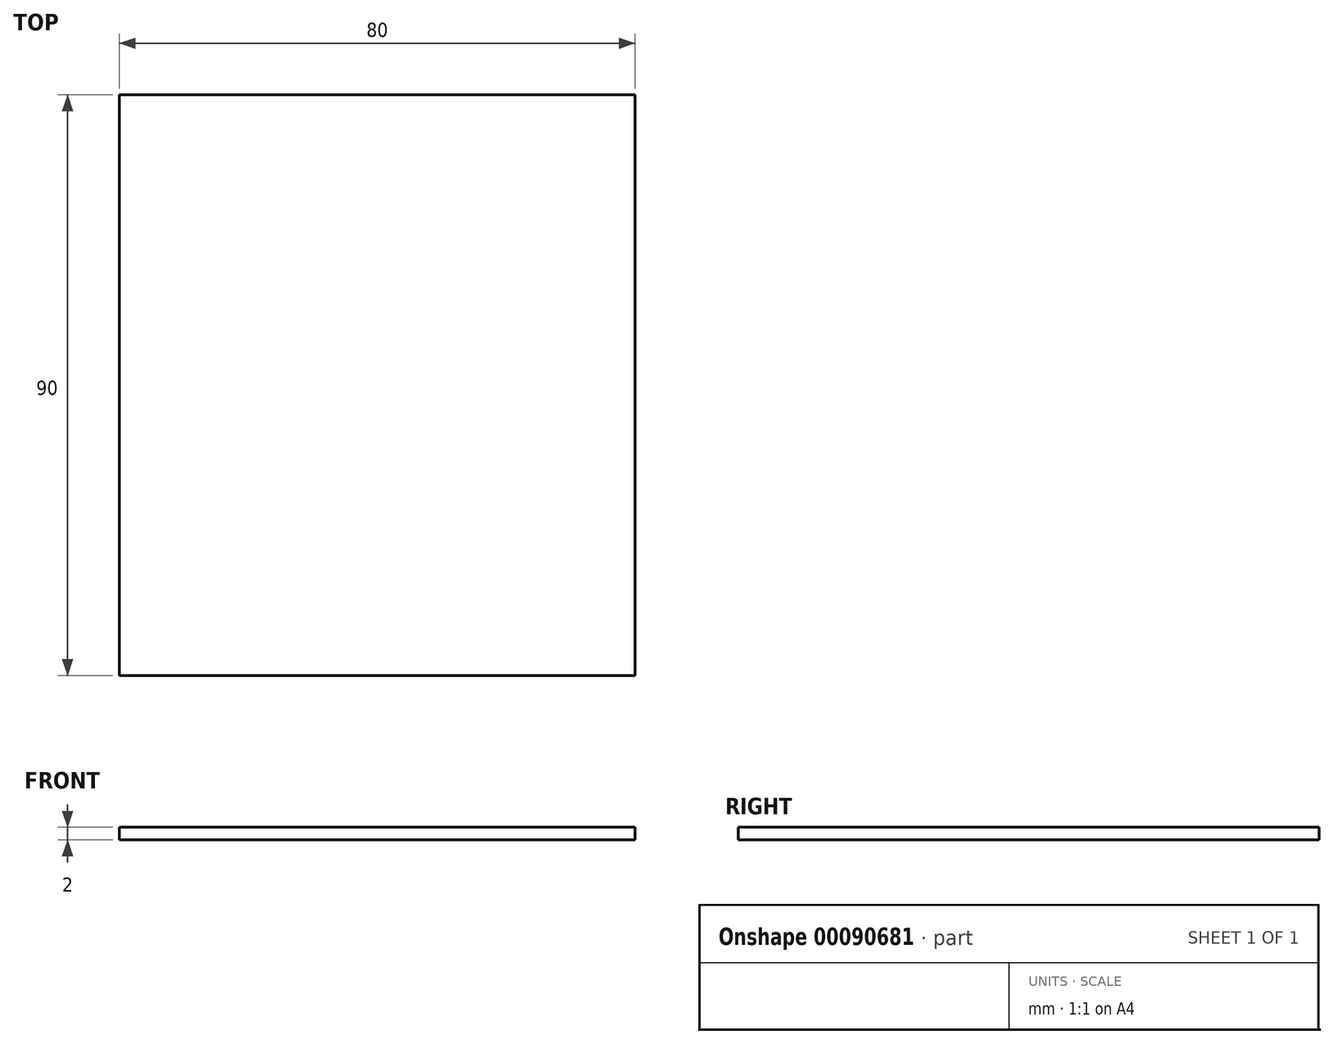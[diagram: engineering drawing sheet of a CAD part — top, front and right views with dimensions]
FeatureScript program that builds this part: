
annotation { "Feature Type Name" : "Feature", "Feature Type Description" : "" }
export const myFeature = defineFeature(function(context is Context, id is Id, definition is map)
    precondition{}
    {
        {
            var Q0;
            Q0=qCreatedBy(makeId("Top.planeOp"),FACE);
            var sketch = newSketch(context, id + "F0", { "sketchPlane" : qUnion([Q0])});
            skLineSegment(sketch, "E0.bottom", {"start": v(-39.72, 48.1) * mm, "end": v(40.28, 48.1) * mm});
            skLineSegment(sketch, "E0.top", {"start": v(-39.72, -41.9) * mm, "end": v(40.28, -41.9) * mm});
            skLineSegment(sketch, "E0.left", {"start": v(-39.72, 48.1) * mm, "end": v(-39.72, -41.9) * mm});
            skLineSegment(sketch, "E0.right", {"start": v(40.28, 48.1) * mm, "end": v(40.28, -41.9) * mm});
            skSolve(sketch);
        }
        {
            var Q0;
            Q0=makeQuery(id+"F0.imprint","IMPRINT",FACE,{"disambiguationData":[TD([[makeQuery(id+"F0.imprint","IMPRINT",EDGE,{"derivedFrom":sQuery(id+"F0.wireOp",EDGE,"E0.bottom")}),-1.0]])]});
            extrude(context, id + "F1", {"entities" : qUnion([Q0]), "depth" : 2 * mm});
        }
    });
